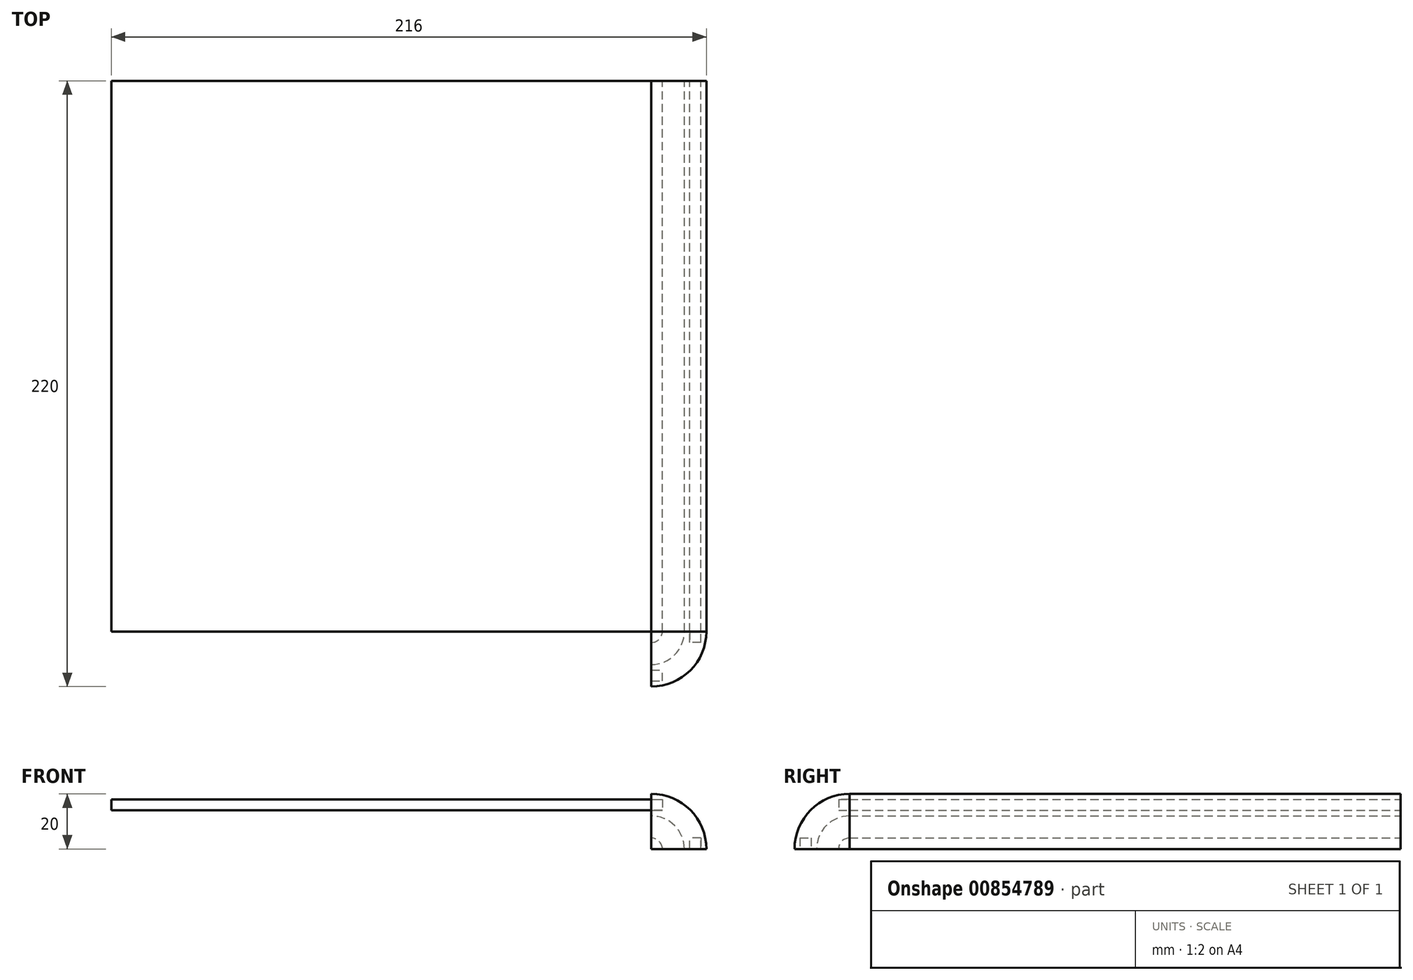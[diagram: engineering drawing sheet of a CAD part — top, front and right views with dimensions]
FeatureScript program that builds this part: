
annotation { "Feature Type Name" : "Feature", "Feature Type Description" : "" }
export const myFeature = defineFeature(function(context is Context, id is Id, definition is map)
    precondition{}
    {
        {
            var Q0;
            Q0=qCreatedBy(makeId("Top.planeOp"),FACE);
            var sketch = newSketch(context, id + "F0", { "sketchPlane" : qUnion([Q0])});
            skLineSegment(sketch, "E0.bottom", {"start": v(-100, 100) * mm, "end": v(100, 100) * mm});
            skLineSegment(sketch, "E0.top", {"start": v(-100, -100) * mm, "end": v(100, -100) * mm});
            skLineSegment(sketch, "E0.left", {"start": v(-100, 100) * mm, "end": v(-100, -100) * mm});
            skLineSegment(sketch, "E0.right", {"start": v(100, 100) * mm, "end": v(100, -100) * mm});
            skSolve(sketch);
        }
        {
            var Q0;
            Q0=makeQuery(id+"F0.imprint","IMPRINT",FACE,{"disambiguationData":[TD([[makeQuery(id+"F0.imprint","IMPRINT",EDGE,{"derivedFrom":sQuery(id+"F0.wireOp",EDGE,"E0.bottom")}),-1.0]])]});
            extrude(context, id + "F1", {"entities" : qUnion([Q0]), "depth" : 4 * mm, "offsetDistance" : 25 * mm});
        }
        {
            var Q0;
            Q0=qCreatedBy(makeId("Front.planeOp"),FACE);
            var sketch = newSketch(context, id + "F2", { "sketchPlane" : qUnion([Q0])});
            skArc(sketch, "E1", {"start": v(116, -14) * mm, "mid": v(110.14, 0.14) * mm, "end": v(96, 6) * mm});
            skLineSegment(sketch, "E2", {"start": v(96, 6) * mm, "end": v(96, 4) * mm});
            skLineSegment(sketch, "E3", {"start": v(96, 4) * mm, "end": v(100, 4) * mm});
            skLineSegment(sketch, "E4", {"start": v(100, 4) * mm, "end": v(100, 0) * mm});
            skLineSegment(sketch, "E5", {"start": v(100, 0) * mm, "end": v(96, 0) * mm});
            skLineSegment(sketch, "E6", {"start": v(96, 0) * mm, "end": v(96, -2) * mm});
            skLineSegment(sketch, "E7", {"start": v(96, -14) * mm, "end": v(113.67, 3.67) * mm, "construction": true});
            skLineSegment(sketch, "E8", {"start": v(96, -14) * mm, "end": v(116, -14) * mm, "construction": true});
            skLineSegment(sketch, "E9", {"start": v(96, -14) * mm, "end": v(96, 6) * mm, "construction": true});
            skArc(sketch, "E10", {"start": v(96, -2) * mm, "mid": v(104.49, -5.51) * mm, "end": v(108, -14) * mm});
            skLineSegment(sketch, "E11.MirrorCS", {"start": v(114, -14) * mm, "end": v(114, -10) * mm});
            skLineSegment(sketch, "E12.MirrorCS", {"start": v(114, -10) * mm, "end": v(110, -10) * mm});
            skLineSegment(sketch, "E13.MirrorCS", {"start": v(110, -10) * mm, "end": v(110, -14) * mm});
            skLineSegment(sketch, "E14", {"start": v(110, -14) * mm, "end": v(108, -14) * mm});
            skLineSegment(sketch, "E15", {"start": v(114, -14) * mm, "end": v(116, -14) * mm});
            skLineSegment(sketch, "E16.0", {"start": v(-100, 4) * mm, "end": v(100, 4) * mm});
            skLineSegment(sketch, "E17.0", {"start": v(-100, 0) * mm, "end": v(100, 0) * mm});
            skSolve(sketch);
        }
        {
            var Q0;
            Q0=makeQuery(id+"F2.imprint","IMPRINT",FACE,{"disambiguationData":[TD([[makeQuery(id+"F2.imprint","IMPRINT",EDGE,{"derivedFrom":sQuery(id+"F2.wireOp",EDGE,"E1")}),1.0]])]});
            extrude(context, id + "F3", {"entities" : qUnion([Q0]), "endBound" : BoundingType.SYMMETRIC, "depth" : 200 * mm, "offsetDistance" : 25 * mm});
        }
        {
            var Q0;
            Q0=makeQuery(id+"F3.opExtrude","CAP_FACE",FACE,{"disambiguationData":[OSD([sQuery(id+"F2.wireOp",EDGE,"E1"),sQuery(id+"F2.wireOp",EDGE,"E2"),sQuery(id+"F2.wireOp",EDGE,"E3"),sQuery(id+"F2.wireOp",EDGE,"E4"),sQuery(id+"F2.wireOp",EDGE,"E5"),sQuery(id+"F2.wireOp",EDGE,"E6"),sQuery(id+"F2.wireOp",EDGE,"E10"),sQuery(id+"F2.wireOp",EDGE,"E11.MirrorCS"),sQuery(id+"F2.wireOp",EDGE,"E12.MirrorCS"),sQuery(id+"F2.wireOp",EDGE,"E13.MirrorCS"),sQuery(id+"F2.wireOp",EDGE,"E14"),sQuery(id+"F2.wireOp",EDGE,"E15")])],"isStart":false});
            var sketch = newSketch(context, id + "F4", { "sketchPlane" : qUnion([Q0])});
            skLineSegment(sketch, "E18", {"start": v(114, -14) * mm, "end": v(110, -14) * mm});
            skSolve(sketch);
        }
        {
            var Q0;
            Q0=makeQuery(id+"F4.imprint","IMPRINT",FACE,{"disambiguationData":[TD([[makeQuery(id+"F4.imprint","IMPRINT",EDGE,{"derivedFrom":makeQuery(id+"F3.opExtrude","CAP_EDGE",EDGE,{"disambiguationData":[OSD([sQuery(id+"F2.wireOp",EDGE,"E1")])],"isStart":false})}),1.0]])]});
            var Q1;
            Q1=makeQuery(id+"F4.imprint","IMPRINT",FACE,{"disambiguationData":[TD([[makeQuery(id+"F4.imprint","IMPRINT",EDGE,{"derivedFrom":sQuery(id+"F4.wireOp",EDGE,"E18")}),-1.0]])]});
            var Q2;
            Q2=makeQuery(id+"F3.opExtrude","CAP_EDGE",EDGE,{"disambiguationData":[OSD([sQuery(id+"F2.wireOp",EDGE,"E2")])],"isStart":false});
            revolve(context, id + "F5", {"surfaceOperationType" : NewSurfaceOperationType.NEW, "entities" : qUnion([Q0, Q1]), "axis" : qUnion([Q2]), "revolveType" : RevolveType.ONE_DIRECTION, "angle" : 90 * degree});
        }
        {
            var Q0;
            Q0=makeQuery(id+"F5.opRevolve","CAP_FACE",FACE,{"disambiguationData":[OSD([sQuery(id+"F2.wireOp",EDGE,"E1"),sQuery(id+"F2.wireOp",EDGE,"E2"),sQuery(id+"F2.wireOp",EDGE,"E3"),sQuery(id+"F2.wireOp",EDGE,"E4"),sQuery(id+"F2.wireOp",EDGE,"E5"),sQuery(id+"F2.wireOp",EDGE,"E6"),sQuery(id+"F2.wireOp",EDGE,"E10"),sQuery(id+"F2.wireOp",EDGE,"E14"),sQuery(id+"F2.wireOp",EDGE,"E15"),sQuery(id+"F4.wireOp",EDGE,"E18")])],"isStart":false});
            var sketch = newSketch(context, id + "F6", { "sketchPlane" : qUnion([Q0])});
            skPoint(sketch, "E19.0", {"position": v(100, -14) * mm});
            skLineSegment(sketch, "E20", {"start": v(100, -14) * mm, "end": v(117.62, 3.62) * mm, "construction": true});
            skLineSegment(sketch, "E21.0", {"start": v(100, 4) * mm, "end": v(104, 4) * mm});
            skLineSegment(sketch, "E22.0", {"start": v(104, 4) * mm, "end": v(104, 0) * mm});
            skLineSegment(sketch, "E23.0", {"start": v(100, 0) * mm, "end": v(104, 0) * mm});
            skLineSegment(sketch, "E24.0", {"start": v(100, 0) * mm, "end": v(100, -2) * mm});
            skLineSegment(sketch, "E25.0", {"start": v(100, 6) * mm, "end": v(100, 4) * mm});
            skLineSegment(sketch, "E26.MirrorCS", {"start": v(118, -10) * mm, "end": v(114, -10) * mm});
            skLineSegment(sketch, "E27.MirrorCS", {"start": v(118, -14) * mm, "end": v(118, -10) * mm});
            skLineSegment(sketch, "E28.MirrorCS", {"start": v(114, -14) * mm, "end": v(114, -10) * mm});
            skLineSegment(sketch, "E29.MirrorCS", {"start": v(114, -14) * mm, "end": v(112, -14) * mm});
            skLineSegment(sketch, "E30.MirrorCS", {"start": v(120, -14) * mm, "end": v(118, -14) * mm});
            skArc(sketch, "E31.0", {"start": v(120, -14) * mm, "mid": v(114.14, 0.14) * mm, "end": v(100, 6) * mm});
            skSolve(sketch);
        }
        {
            var Q0;
            Q0=makeQuery(id+"F6.imprint","IMPRINT",FACE,{"disambiguationData":[TD([[makeQuery(id+"F6.imprint","IMPRINT",EDGE,{"derivedFrom":sQuery(id+"F6.wireOp",EDGE,"E26.MirrorCS")}),1.0]])]});
            var Q1;
            Q1=sQuery(id+"F6.wireOp",EDGE,"E29.MirrorCS");
            revolve(context, id + "F7", {"operationType" : NewBodyOperationType.REMOVE, "surfaceOperationType" : NewSurfaceOperationType.NEW, "entities" : qUnion([Q0]), "axis" : qUnion([Q1]), "revolveType" : RevolveType.FULL, "oppositeDirection" : true});
        }
        {
            var Q0;
            Q0=makeQuery(id+"F3.opExtrude","CAP_FACE",FACE,{"disambiguationData":[OSD([sQuery(id+"F2.wireOp",EDGE,"E1"),sQuery(id+"F2.wireOp",EDGE,"E2"),sQuery(id+"F2.wireOp",EDGE,"E3"),sQuery(id+"F2.wireOp",EDGE,"E4"),sQuery(id+"F2.wireOp",EDGE,"E5"),sQuery(id+"F2.wireOp",EDGE,"E6"),sQuery(id+"F2.wireOp",EDGE,"E10"),sQuery(id+"F2.wireOp",EDGE,"E11.MirrorCS"),sQuery(id+"F2.wireOp",EDGE,"E12.MirrorCS"),sQuery(id+"F2.wireOp",EDGE,"E13.MirrorCS"),sQuery(id+"F2.wireOp",EDGE,"E14"),sQuery(id+"F2.wireOp",EDGE,"E15")])],"isStart":false});
            var sketch = newSketch(context, id + "F8", { "sketchPlane" : qUnion([Q0])});
            skLineSegment(sketch, "E32.0", {"start": v(114, -10) * mm, "end": v(110, -10) * mm});
            skLineSegment(sketch, "E33.0", {"start": v(114, -14) * mm, "end": v(114, -10) * mm});
            skLineSegment(sketch, "E34.0", {"start": v(110, -10) * mm, "end": v(110, -14) * mm});
            skLineSegment(sketch, "E35", {"start": v(110, -14) * mm, "end": v(114, -14) * mm});
            skSolve(sketch);
        }
        {
            var Q0;
            Q0=makeQuery(id+"F8.imprint","IMPRINT",FACE,{"disambiguationData":[TD([[makeQuery(id+"F8.imprint","IMPRINT",EDGE,{"derivedFrom":sQuery(id+"F8.wireOp",EDGE,"E32.0")}),1.0]])]});
            var Q1;
            Q1=makeQuery(id+"F3.opExtrude","CAP_EDGE",EDGE,{"disambiguationData":[OSD([sQuery(id+"F2.wireOp",EDGE,"E14")])],"isStart":false});
            revolve(context, id + "F9", {"operationType" : NewBodyOperationType.REMOVE, "surfaceOperationType" : NewSurfaceOperationType.NEW, "entities" : qUnion([Q0]), "axis" : qUnion([Q1]), "revolveType" : RevolveType.FULL, "oppositeDirection" : true});
        }
    });
